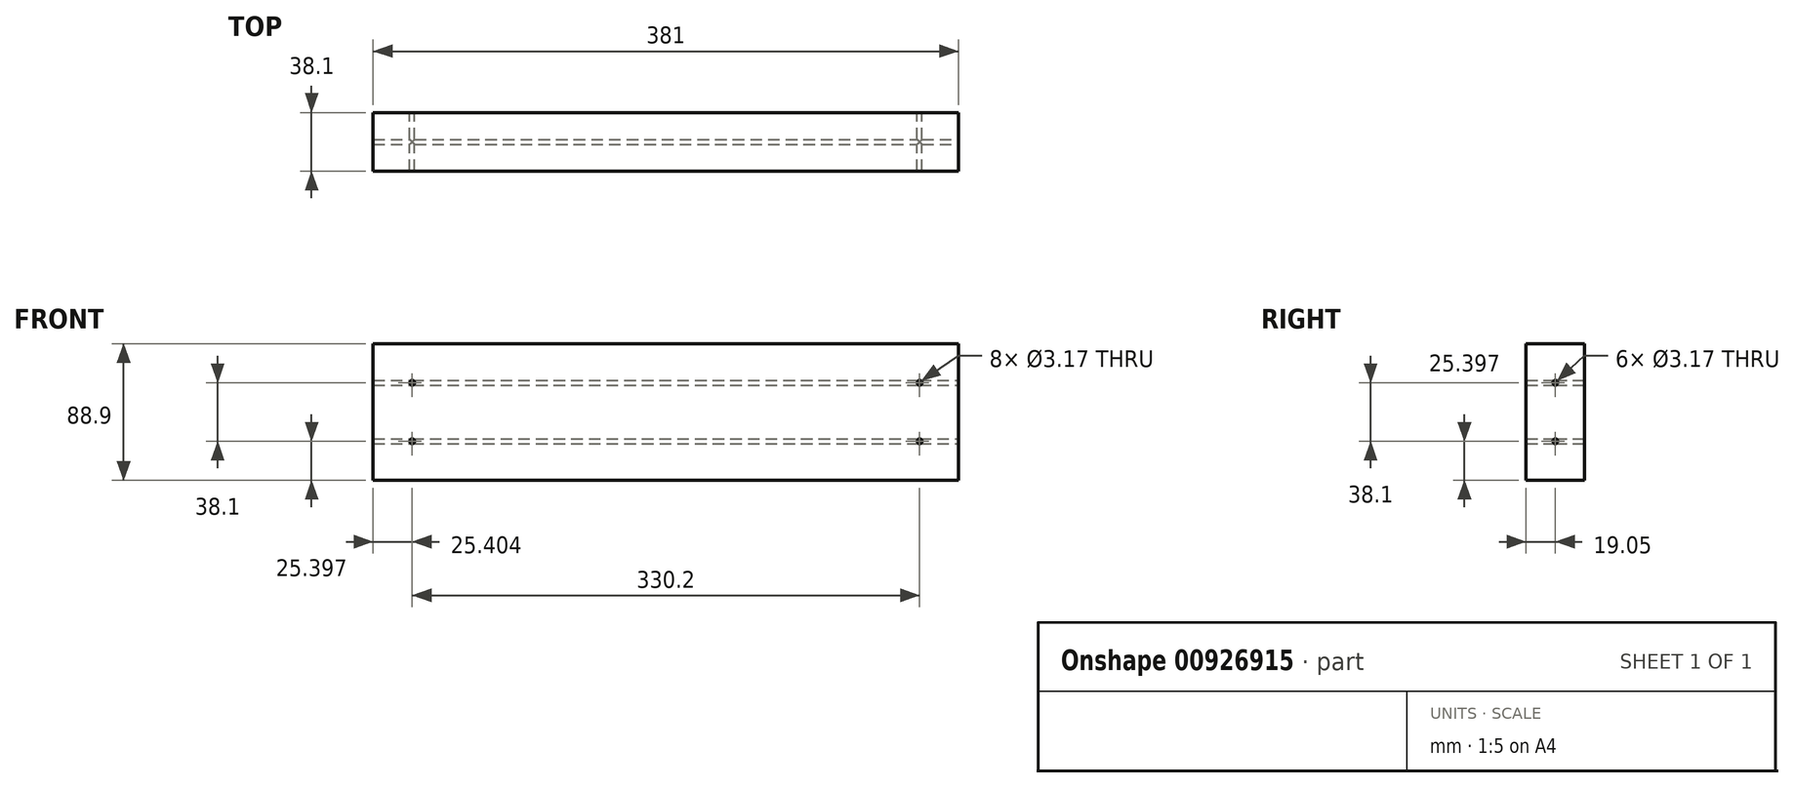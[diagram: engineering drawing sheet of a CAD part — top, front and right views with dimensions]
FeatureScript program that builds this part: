
annotation { "Feature Type Name" : "Feature", "Feature Type Description" : "" }
export const myFeature = defineFeature(function(context is Context, id is Id, definition is map)
    precondition{}
    {
        {
            var Q0;
            Q0=qCreatedBy(makeId("Front.planeOp"),FACE);
            var sketch = newSketch(context, id + "F0", { "sketchPlane" : qUnion([Q0])});
            skLineSegment(sketch, "E0.bottom", {"start": v(-112.7, 108.74) * mm, "end": v(268.3, 108.74) * mm});
            skLineSegment(sketch, "E0.top", {"start": v(-112.7, 19.84) * mm, "end": v(268.3, 19.84) * mm});
            skLineSegment(sketch, "E0.left", {"start": v(-112.7, 108.74) * mm, "end": v(-112.7, 19.84) * mm});
            skLineSegment(sketch, "E0.right", {"start": v(268.3, 108.74) * mm, "end": v(268.3, 19.84) * mm});
            skSolve(sketch);
        }
        {
            var Q0;
            Q0=makeQuery(id+"F0.imprint","IMPRINT",FACE,{"disambiguationData":[TD([[makeQuery(id+"F0.imprint","IMPRINT",EDGE,{"derivedFrom":sQuery(id+"F0.wireOp",EDGE,"E0.bottom")}),-1.0]])]});
            extrude(context, id + "F1", {"entities" : qUnion([Q0]), "depth" : 38.1 * mm, "offsetDistance" : 25.4 * mm});
        }
        {
            var Q0;
            Q0=makeQuery(id+"F1.opExtrude","SWEPT_FACE",FACE,{"disambiguationData":[OSD([sQuery(id+"F0.wireOp",EDGE,"E0.right")])]});
            var sketch = newSketch(context, id + "F2", { "sketchPlane" : qUnion([Q0])});
            skLineSegment(sketch, "E1", {"start": v(-19.05, 108.74) * mm, "end": v(-19.05, 19.84) * mm, "construction": true});
            skPoint(sketch, "E2", {"position": v(-19.05, 83.34) * mm});
            skPoint(sketch, "E3", {"position": v(-19.05, 45.24) * mm});
            skSolve(sketch);
        }
        {
            var Q0;
            Q0=sQuery(id+"F2.wireOp",VERTEX,"E2");
            var Q1;
            Q1=sQuery(id+"F2.wireOp",VERTEX,"E3");
            var Q2;
            Q2=makeQuery(id+"F1.opExtrude","SWEPT_BODY",BODY,{"disambiguationData":[OSD([sQuery(id+"F0.wireOp",EDGE,"E0.bottom"),sQuery(id+"F0.wireOp",EDGE,"E0.top"),sQuery(id+"F0.wireOp",EDGE,"E0.left"),sQuery(id+"F0.wireOp",EDGE,"E0.right")])]});
            hole(context, id + "F3", {"style" : HoleStyle.SIMPLE, "endStyle" : HoleEndStyle.THROUGH, "holeDiameter" : 3.17 * mm, "majorDiameter" : 6.35 * mm, "isTappedThrough" : true, "tappedDepth" : 12.7 * mm, "tapClearance" : 3, "locations" : qUnion([Q0, Q1]), "scope" : qUnion([Q2])});
        }
        {
            var Q0;
            Q0=makeQuery(id+"F1.opExtrude","CAP_FACE",FACE,{"disambiguationData":[OSD([sQuery(id+"F0.wireOp",EDGE,"E0.bottom"),sQuery(id+"F0.wireOp",EDGE,"E0.top"),sQuery(id+"F0.wireOp",EDGE,"E0.left"),sQuery(id+"F0.wireOp",EDGE,"E0.right")])],"isStart":true});
            var sketch = newSketch(context, id + "F4", { "sketchPlane" : qUnion([Q0])});
            skLineSegment(sketch, "E4", {"start": v(-77.8, 108.74) * mm, "end": v(-77.8, 19.84) * mm, "construction": true});
            skLineSegment(sketch, "E5", {"start": v(87.3, 108.74) * mm, "end": v(87.3, 19.84) * mm, "construction": true});
            skPoint(sketch, "E6", {"position": v(87.3, 83.34) * mm});
            skPoint(sketch, "E7", {"position": v(87.3, 45.24) * mm});
            skPoint(sketch, "E8.MirrorP", {"position": v(-242.9, 83.34) * mm});
            skPoint(sketch, "E9.MirrorP", {"position": v(-242.9, 45.24) * mm});
            skSolve(sketch);
        }
        {
            var Q0;
            Q0=sQuery(id+"F4.wireOp",VERTEX,"E8.MirrorP");
            var Q1;
            Q1=sQuery(id+"F4.wireOp",VERTEX,"E9.MirrorP");
            var Q2;
            Q2=sQuery(id+"F4.wireOp",VERTEX,"E6");
            var Q3;
            Q3=sQuery(id+"F4.wireOp",VERTEX,"E7");
            var Q4;
            Q4=makeQuery(id+"F1.opExtrude","SWEPT_BODY",BODY,{"disambiguationData":[OSD([sQuery(id+"F0.wireOp",EDGE,"E0.bottom"),sQuery(id+"F0.wireOp",EDGE,"E0.top"),sQuery(id+"F0.wireOp",EDGE,"E0.left"),sQuery(id+"F0.wireOp",EDGE,"E0.right")])]});
            hole(context, id + "F5", {"style" : HoleStyle.SIMPLE, "endStyle" : HoleEndStyle.THROUGH, "holeDiameter" : 3.17 * mm, "majorDiameter" : 6.35 * mm, "isTappedThrough" : true, "tappedDepth" : 12.7 * mm, "tapClearance" : 3, "locations" : qUnion([Q0, Q1, Q2, Q3]), "scope" : qUnion([Q4])});
        }
    });
